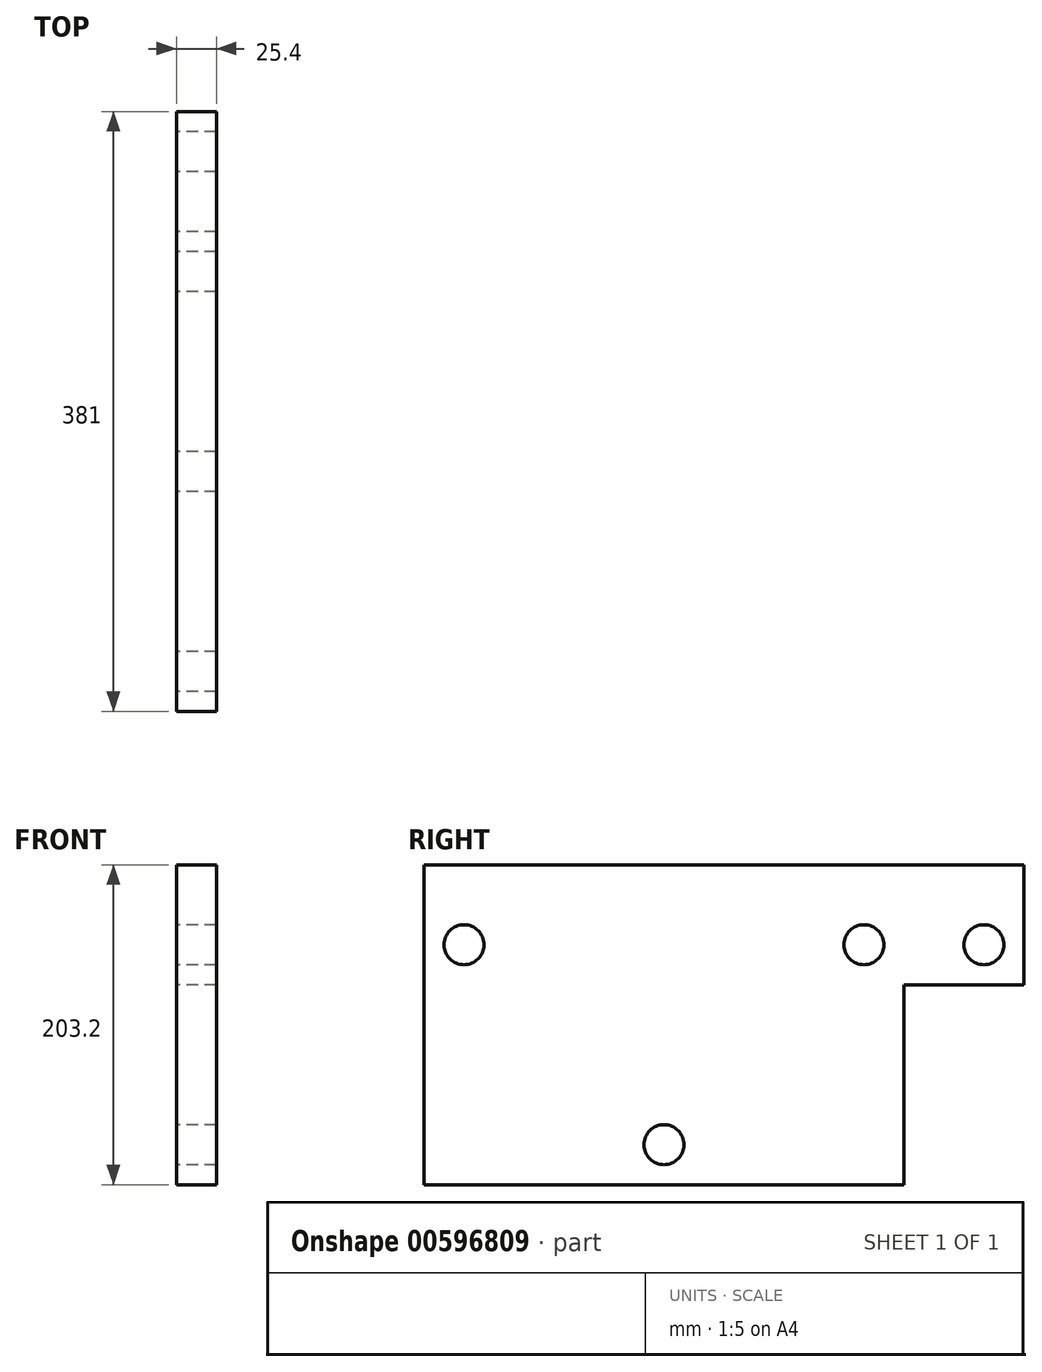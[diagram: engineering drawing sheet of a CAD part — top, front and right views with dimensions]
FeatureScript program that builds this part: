
annotation { "Feature Type Name" : "Feature", "Feature Type Description" : "" }
export const myFeature = defineFeature(function(context is Context, id is Id, definition is map)
    precondition{}
    {
        {
            var Q0;
            Q0=qCreatedBy(makeId("Right.planeOp"),FACE);
            var sketch = newSketch(context, id + "F0", { "sketchPlane" : qUnion([Q0])});
            skLineSegment(sketch, "E0.bottom", {"start": v(0, 0) * mm, "end": v(304.8, 0) * mm});
            skLineSegment(sketch, "E0.top", {"start": v(0, -203.2) * mm, "end": v(304.8, -203.2) * mm});
            skLineSegment(sketch, "E0.left", {"start": v(0, 0) * mm, "end": v(0, -203.2) * mm});
            skLineSegment(sketch, "E0.right", {"start": v(304.8, 0) * mm, "end": v(304.8, -203.2) * mm});
            skCircle(sketch, "E1", {"center": v(25.4, -50.8) * mm, "radius": 12.7 * mm});
            skCircle(sketch, "E2", {"center": v(279.4, -50.8) * mm, "radius": 12.7 * mm});
            skCircle(sketch, "E3", {"center": v(152.4, -177.8) * mm, "radius": 12.7 * mm});
            skLineSegment(sketch, "E4", {"start": v(304.8, 0) * mm, "end": v(381, 0) * mm});
            skLineSegment(sketch, "E5", {"start": v(381, 0) * mm, "end": v(381, -76.2) * mm});
            skLineSegment(sketch, "E6", {"start": v(381, -76.2) * mm, "end": v(304.8, -76.2) * mm});
            skCircle(sketch, "E7", {"center": v(355.6, -50.8) * mm, "radius": 12.7 * mm});
            skSolve(sketch);
        }
        {
            var Q0;
            Q0 = qSketchRegion(id + "F0", true);
            extrude(context, id + "F1", {"entities" : qUnion([Q0]), "depth" : 25.4 * mm, "offsetDistance" : 25.4 * mm});
        }
    });
